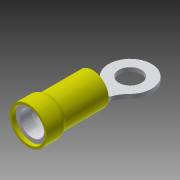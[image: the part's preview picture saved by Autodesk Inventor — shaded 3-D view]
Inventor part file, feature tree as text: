
AUTODESK INVENTOR PART (.ipt)
format: ipt  version: 2014 (Build 180170000, 170)  size: 420,864 bytes
history: native  units: in
note: dims shown in document units (in); Inventor stores cm internally (conversion verified against a paired STEP export)
features: sketch x6, fillet x5, extrude x4, projected_geometry x4, shell x1, revolve x1, plane x1, loft x1, chamfer x1, other x1
ambient origin geometry x8: Origin, YZ Plane, XZ Plane, XY Plane, X Axis, Y Axis, Z Axis, Center Point
bodies: Solid1 (feature_tree), Solid2 (feature_tree)
feature tree (25):
  extrude  "Extrusion1"  Depth=0.5595in TaperAngle=0.0deg
  extrude  "Extrusion2"  Depth=0.157in TaperAngle=0.0deg
  fillet  "Fillet1"  Radius=0.05in
  shell  "Shell1"  Thickness=0.02in
  revolve  "Revolution1"  [1 undecoded]
  plane  "Work Plane1"
  extrude  "Extrusion3"  [1 undecoded]
  loft  "Loft1"
  fillet  "Fillet2"  Radius=0.327in
  fillet  "Fillet3"  Radius=0.087in
  fillet  "Fillet4"  Radius=0.036in
  fillet  "Fillet5"  [1 undecoded]
  chamfer  "Chamfer1"  Angle=90.0deg  [1 undecoded]
  extrude  "Extrusion4"  Depth=0.036in
  sketch  "Sketch1"  dims[d0=0.2785in d1=0.5595in d2=0.0in]
  sketch  "Sketch2"  dims[d3=0.324in d4=0.157in d5=0.0in d6=0.05in d7=0.02in]
  projected_geometry  "Projected Loop1"
  sketch  "Sketch3"  dims[d9=0.035in d10=0.035in]
  sketch  "Sketch4"  dims[d11=90.0deg d12=-0.108in]
  sketch  "Sketch5"  dims[d13=0.3745in d14=0.089in d15=0.327in d16=0.087in d17=0.036in d18=0.0in d19=0.0in d20=90.0deg d21=0.0in d22=90.0deg]
  projected_geometry  "Projected Loop2"
  other  "Edges1"
  sketch  "Sketch6"  dims[d23=0.04in d24=0.04in d25=0.04in d26=0.04in d27=0.003in d28=0.125in d29=45.0deg d30=0.005in d31=0.036in d32=0.0in]
  projected_geometry  "Project Cut Edges1"
  projected_geometry  "Project Cut Edges2"
note: 4 required parameter values undecoded (feature->parameter linkage not recoverable at this tier; creation-order binding heuristic only, values carry confidence <= 0.55)